# Revit family: JOMA_Knagge
name_source: partatom
category: Structural Connections
revit_build: Autodesk Revit Structure 2012 (Build: 20110309_2315(x64)
units: mm (PartAtom-declared; Revit-internal decimal feet)

## types (3) — shared parameters
Default Elevation = 1219 mm
Länk Joma Dimensioneringsverktyg = http://www.joma.se
Material = Varmförzinkad stålplåt
f = 9 mm  [stored 0.0295276 ft]

## per-type parameters (varying)
| type | Grader | Typ | Typ 130 | Typ 170 | Typ 210 | Vikt | b | d | e | fläns | g | h | höjd | i |
| 5400210 | 8.85° | TYP 210 | No | No | Yes | 0.96 | 8 mm  [stored 0.0262467 ft] | 50 mm | 54 mm | 16 mm  [stored 0.0524934 ft] | 23 mm | 19 mm | 210 mm | 3 mm  [stored 0.00984252 ft] |
| 5400170 | 8.85° | TYP 170 | No | Yes | No | 0.55 | 8 mm  [stored 0.0262467 ft] | 50 mm | 45 mm | 16 mm  [stored 0.0524934 ft] | 23 mm | 19 mm | 155 mm | 3 mm  [stored 0.00984252 ft] |
| 5400130 | 16.50° | TYP 130 | Yes | No | No | 0.39 | 7 mm  [stored 0.0229659 ft] | 24 mm | 53 mm | 15 mm  [stored 0.0492126 ft] | 20 mm  [stored 0.0656168 ft] | 10 mm  [stored 0.0328084 ft] | 130 mm  [stored 0.426509 ft] | 18 mm |

note: [stored X ft] marks values corroborated as IEEE doubles in the binary element streams (Revit-internal decimal feet)

## geometry (parser evidence)
native form markers: Sweep x3
no freeform markers — native parametric forms only
